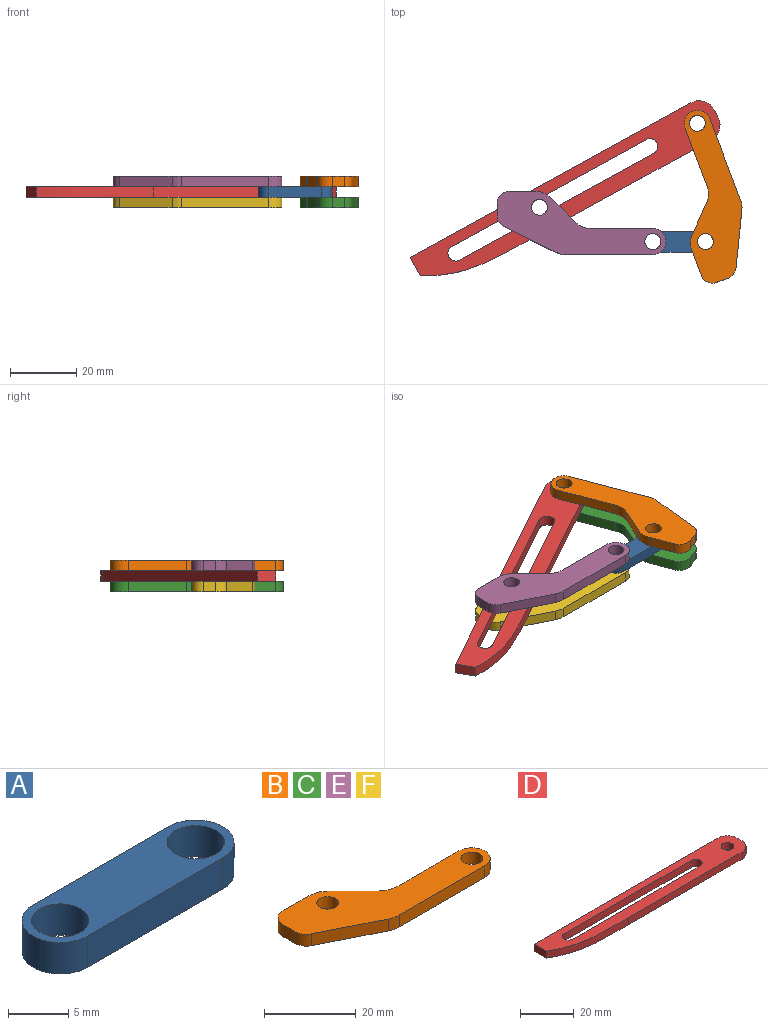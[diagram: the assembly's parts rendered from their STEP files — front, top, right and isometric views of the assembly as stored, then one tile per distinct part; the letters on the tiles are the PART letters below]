
ASSEMBLY  parts=6 mates=8
PART A: 8 faces, bbox 22.2x6.4x3.2 mm
  f0: plane 15.88x3.18mm, normal (0,-1,0), area 50.4mm2, adj f4,f5,f6,f7
  f1: cylinder r=2.38mm len=4.76mm, axis (0,0,-1), area 47.5mm2, adj f4,f5
  f2: plane 15.88x3.18mm, normal (0,1,0), area 50.4mm2, adj f4,f5,f6,f7
  f3: cylinder r=2.38mm len=4.76mm, axis (0,0,-1), area 47.5mm2, adj f4,f5
  f4: plane 22.23x6.35mm, normal (0,0,1), area 96.8mm2, adj f0,f1,f2,f3,f6,f7
  f5: plane 22.23x6.35mm, normal (0,0,-1), area 96.8mm2, adj f0,f1,f2,f3,f6,f7
  f6: cylinder r=3.17mm len=6.35mm, axis (0,0,-1), area 31.7mm2, adj f0,f2,f4,f5
  f7: cylinder r=3.17mm len=6.35mm, axis (0,0,1), area 31.7mm2, adj f0,f2,f4,f5
PART B: 16 faces, bbox 50.8x19.1x3.2 mm
  f0: plane 8.06x3.18mm, normal (0,1,0), area 25.6mm2, adj f9,f10,f13,f14
  f1: plane 3.7x3.18mm, normal (-1,0,0), area 11.7mm2, adj f9,f10,f14,f15
  f2: plane 15.72x7.86mm, normal (-0.45,-0.89,0), area 55.8mm2, adj f9,f10,f11,f15
  f3: plane 26.28x3.18mm, normal (0,-1,0), area 83.4mm2, adj f4,f9,f10,f11
  f4: cylinder r=3.97mm len=7.94mm, axis (0,0,-1), area 39.6mm2, adj f3,f5,f9,f10
  f5: plane 18.8x3.18mm, normal (0,1,0), area 59.7mm2, adj f4,f9,f10,f12
  f6: cylinder r=2.38mm len=4.76mm, axis (0,0,-1), area 47.5mm2, adj f9,f10
  f7: plane 7.39x7.39mm, normal (0.71,0.71,0), area 33.2mm2, adj f9,f10,f12,f13
  f8: cylinder r=2.38mm len=4.76mm, axis (0,0,-1), area 47.5mm2, adj f9,f10
  f9: plane 50.8x19.05mm, normal (0,0,1), area 486.8mm2, adj f0,f1,f2,f3,f4,f5,f6,f7
  f10: plane 50.8x19.05mm, normal (0,0,-1), area 486.8mm2, adj f0,f1,f2,f3,f4,f5,f6,f7
  f11: cylinder r=6.35mm len=3.18mm, axis (0,0,-1), area 9.3mm2, adj f2,f3,f9,f10
  f12: cylinder r=6.35mm len=4.49mm, axis (0,0,1), area 15.8mm2, adj f5,f7,f9,f10
  f13: cylinder r=6.35mm len=4.49mm, axis (0,0,-1), area 15.8mm2, adj f0,f7,f9,f10
  f14: cylinder r=3.6mm len=3.6mm, axis (0,0,-1), area 18mm2, adj f0,f1,f9,f10
  f15: cylinder r=3.6mm len=3.22mm, axis (0,0,1), area 12.7mm2, adj f1,f2,f9,f10
PART C: same geometry as B
PART D: 14 faces, bbox 101.6x12.7x3.2 mm
  f0: cylinder r=2.38mm len=4.76mm, axis (0,0,-1), area 23.8mm2, adj f1,f9,f10,f11
  f1: plane 66.68x3.18mm, normal (0,1,0), area 211.7mm2, adj f0,f2,f10,f11
  f2: cylinder r=2.38mm len=4.76mm, axis (0,0,-1), area 23.8mm2, adj f1,f9,f10,f11
  f3: plane 6.35x3.18mm, normal (-1,0,0), area 20.2mm2, adj f4,f8,f10,f11
  f4: extruded ~36.79x6.35mm, area 120.3mm2, adj f3,f5,f10,f11
  f5: plane 59.73x3.18mm, normal (0,-1,0), area 189.6mm2, adj f4,f10,f11,f12
  f6: plane 3.18x2.54mm, normal (1,0,0), area 8.1mm2, adj f10,f11,f12,f13
  f7: cylinder r=2.38mm len=4.76mm, axis (0,0,-1), area 47.5mm2, adj f10,f11
  f8: plane 96.52x3.18mm, normal (0,1,0), area 306.5mm2, adj f3,f10,f11,f13
  f9: plane 66.68x3.18mm, normal (0,-1,0), area 211.7mm2, adj f0,f2,f10,f11
  f10: plane 101.6x12.7mm, normal (0,0,1), area 876.1mm2, adj f0,f1,f2,f3,f4,f5,f6,f7
  f11: plane 101.6x12.7mm, normal (0,0,-1), area 876.1mm2, adj f0,f1,f2,f3,f4,f5,f6,f7
  f12: cylinder r=5.08mm len=5.08mm, axis (0,0,-1), area 25.3mm2, adj f5,f6,f10,f11
  f13: cylinder r=5.08mm len=5.08mm, axis (0,0,1), area 25.3mm2, adj f6,f8,f10,f11
PART E: same geometry as B
PART F: same geometry as B
PLACE A t=(-3.18,0.79,-3.18)mm
PLACE B rot(axis=(0,0,1),110.7deg) t=(33.73,-2.85,0)mm
PLACE C rot(axis=(0,0,1),110.7deg) t=(33.73,-2.85,-6.35)mm
PLACE D rot(axis=(0,0,1),28.8deg) t=(-66.96,-11.92,-3.18)mm
PLACE E t=(-46.83,0,0)mm
PLACE F t=(-46.83,0,-6.35)mm
MATE fastened E.f4 <-> A.f3  axis (0,0,-1) through (0,3.97,0)mm
MATE planar B.f3 <-> C.f3  axis (0.94,0.35,0) through (21.81,28.66,1.59)mm
MATE fastened A.f3 <-> F.f4  axis (0,0,-1) through (0,3.97,-3.18)mm
MATE pin_slot E.f6 <-> D.f2  axis (0,0,-1) through (-34.13,14.29,0)mm
MATE planar C.f2 <-> B.f2  axis (0.99,-0.1,0) through (25.94,4.73,-4.76)mm
MATE planar A.f5 <-> C.f9  axis (0,0,-1) through (7.94,3.97,-3.18)mm
MATE revolute D.f7 <-> B.f4  axis (0,0,1) through (13.44,39.54,0)mm
MATE revolute A.f1 <-> B.f6  axis (0,0,1) through (15.88,3.97,0)mm
